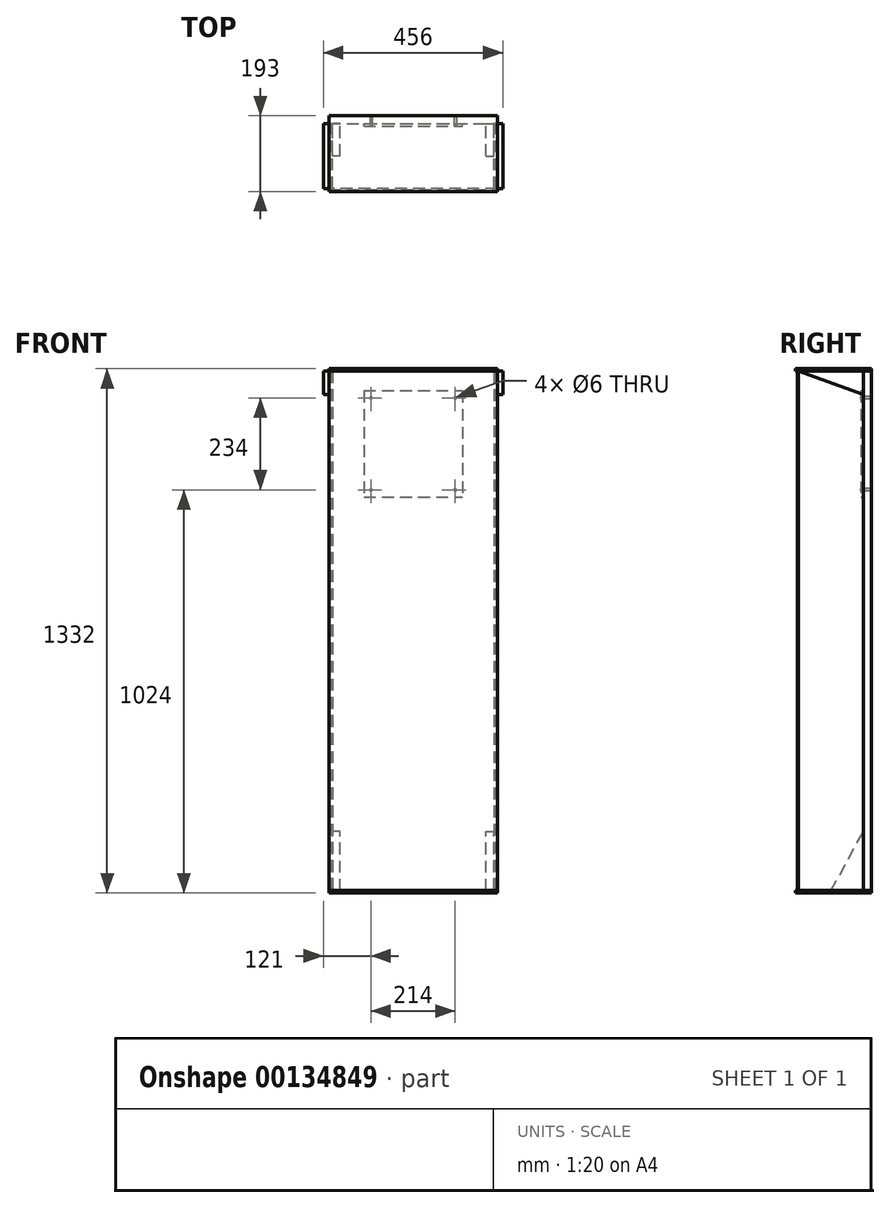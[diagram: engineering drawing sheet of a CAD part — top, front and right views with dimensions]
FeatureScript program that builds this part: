
annotation { "Feature Type Name" : "Feature", "Feature Type Description" : "" }
export const myFeature = defineFeature(function(context is Context, id is Id, definition is map)
    precondition{}
    {
        {
            var Q0;
            Q0=qCreatedBy(makeId("Front.planeOp"),FACE);
            var sketch = newSketch(context, id + "F0", { "sketchPlane" : qUnion([Q0])});
            skLineSegment(sketch, "E0.rect.bottom", {"start": v(-125, 125) * mm, "end": v(125, 125) * mm});
            skLineSegment(sketch, "E0.rect.top", {"start": v(-125, -125) * mm, "end": v(125, -125) * mm});
            skLineSegment(sketch, "E0.rect.left", {"start": v(-125, 125) * mm, "end": v(-125, -125) * mm});
            skLineSegment(sketch, "E0.rect.right", {"start": v(125, 125) * mm, "end": v(125, -125) * mm});
            skPoint(sketch, "E0.rect.middle", {"position": v(0, 0) * mm});
            skSolve(sketch);
        }
        {
            var Q0;
            Q0=qSketchRegion(id+"F0",true);
            extrude(context, id + "F1", {"entities" : qUnion([Q0]), "depth" : 6 * mm});
        }
        {
            var Q0;
            Q0=makeQuery(id+"F1.opExtrude","CAP_FACE",FACE,{"disambiguationData":[OSD([sQuery(id+"F0.wireOp",EDGE,"E0.rect.bottom"),sQuery(id+"F0.wireOp",EDGE,"E0.rect.top"),sQuery(id+"F0.wireOp",EDGE,"E0.rect.left"),sQuery(id+"F0.wireOp",EDGE,"E0.rect.right")])],"isStart":true});
            var sketch = newSketch(context, id + "F2", { "sketchPlane" : qUnion([Q0])});
            skLineSegment(sketch, "E1.rect.bottom", {"start": v(214, 175) * mm, "end": v(-214, 175) * mm});
            skLineSegment(sketch, "E1.rect.top", {"start": v(214, -1145) * mm, "end": v(-214, -1145) * mm});
            skLineSegment(sketch, "E1.rect.left", {"start": v(214, 175) * mm, "end": v(214, -1145) * mm});
            skLineSegment(sketch, "E1.rect.right", {"start": v(-214, 175) * mm, "end": v(-214, -1145) * mm});
            skPoint(sketch, "E1.rect.middle", {"position": v(0, -485) * mm});
            skSolve(sketch);
        }
        {
            var Q0;
            Q0=qSketchRegion(id+"F2",true);
            extrude(context, id + "F3", {"entities" : qUnion([Q0]), "depth" : 20 * mm});
        }
        {
            var Q0;
            Q0=makeQuery(id+"F3.opExtrude","SWEPT_FACE",FACE,{"disambiguationData":[OSD([sQuery(id+"F2.wireOp",EDGE,"E1.rect.bottom")])]});
            var sketch = newSketch(context, id + "F4", { "sketchPlane" : qUnion([Q0])});
            skLineSegment(sketch, "E2.bottom", {"start": v(-214, 20) * mm, "end": v(214, 20) * mm});
            skLineSegment(sketch, "E2.top", {"start": v(-214, -173) * mm, "end": v(214, -173) * mm});
            skLineSegment(sketch, "E2.left", {"start": v(-214, 20) * mm, "end": v(-214, -173) * mm});
            skLineSegment(sketch, "E2.right", {"start": v(214, 20) * mm, "end": v(214, -173) * mm});
            skSolve(sketch);
        }
        {
            var Q0;
            Q0=qSketchRegion(id+"F4",true);
            extrude(context, id + "F5", {"entities" : qUnion([Q0]), "depth" : 6 * mm});
        }
        {
            var Q0;
            Q0=makeQuery(id+"F3.opExtrude","CAP_FACE",FACE,{"disambiguationData":[OSD([sQuery(id+"F2.wireOp",EDGE,"E1.rect.bottom"),sQuery(id+"F2.wireOp",EDGE,"E1.rect.top"),sQuery(id+"F2.wireOp",EDGE,"E1.rect.left"),sQuery(id+"F2.wireOp",EDGE,"E1.rect.right")])],"isStart":true});
            var sketch = newSketch(context, id + "F6", { "sketchPlane" : qUnion([Q0])});
            skLineSegment(sketch, "E3.bottom", {"start": v(-208, 175) * mm, "end": v(-205, 175) * mm});
            skLineSegment(sketch, "E3.top", {"start": v(-208, -1145) * mm, "end": v(-205, -1145) * mm});
            skLineSegment(sketch, "E3.left", {"start": v(-208, 175) * mm, "end": v(-208, -1145) * mm});
            skLineSegment(sketch, "E3.right", {"start": v(-205, 175) * mm, "end": v(-205, -1145) * mm});
            skSolve(sketch);
        }
        {
            var Q0;
            Q0=qSketchRegion(id+"F6",true);
            extrude(context, id + "F7", {"entities" : qUnion([Q0]), "depth" : 165 * mm});
        }
        {
            var Q0;
            Q0=makeQuery(id+"F7.opExtrude","SWEPT_BODY",BODY,{"disambiguationData":[OSD([sQuery(id+"F6.wireOp",EDGE,"E3.bottom"),sQuery(id+"F6.wireOp",EDGE,"E3.top"),sQuery(id+"F6.wireOp",EDGE,"E3.left"),sQuery(id+"F6.wireOp",EDGE,"E3.right")])]});
            var Q1;
            Q1=qCreatedBy(makeId("Right.planeOp"),FACE);
            mirror(context, id + "F8", {"entities" : qUnion([Q0]), "mirrorPlane" : qUnion([Q1])});
        }
        {
            var Q0;
            Q0=makeQuery(id+"F5.opExtrude","CAP_FACE",FACE,{"disambiguationData":[OSD([sQuery(id+"F4.wireOp",EDGE,"E2.bottom"),sQuery(id+"F4.wireOp",EDGE,"E2.top"),sQuery(id+"F4.wireOp",EDGE,"E2.left"),sQuery(id+"F4.wireOp",EDGE,"E2.right")])],"isStart":true});
            var Q1;
            Q1=makeQuery(id+"F3.opExtrude","SWEPT_FACE",FACE,{"disambiguationData":[OSD([sQuery(id+"F2.wireOp",EDGE,"E1.rect.top")])]});
            cPlane(context, id + "F9", {"entities" : qUnion([Q0, Q1]), "cplaneType" : CPlaneType.MID_PLANE, "offset" : 150 * mm, "width" : 150 * mm, "height" : 150 * mm});
        }
        {
            var Q0;
            Q0=makeQuery(id+"F5.opExtrude","SWEPT_BODY",BODY,{"disambiguationData":[OSD([sQuery(id+"F4.wireOp",EDGE,"E2.bottom"),sQuery(id+"F4.wireOp",EDGE,"E2.top"),sQuery(id+"F4.wireOp",EDGE,"E2.left"),sQuery(id+"F4.wireOp",EDGE,"E2.right")])]});
            var Q1;
            Q1=qCreatedBy(id+"F9.planeOp",FACE);
            mirror(context, id + "F10", {"entities" : qUnion([Q0]), "mirrorPlane" : qUnion([Q1])});
        }
        {
            var Q0;
            Q0=makeQuery(id+"F5.opExtrude","CAP_FACE",FACE,{"disambiguationData":[OSD([sQuery(id+"F4.wireOp",EDGE,"E2.bottom"),sQuery(id+"F4.wireOp",EDGE,"E2.top"),sQuery(id+"F4.wireOp",EDGE,"E2.left"),sQuery(id+"F4.wireOp",EDGE,"E2.right")])],"isStart":true});
            var sketch = newSketch(context, id + "F11", { "sketchPlane" : qUnion([Q0])});
            skLineSegment(sketch, "E4.0", {"start": v(-208, 165) * mm, "end": v(-205, 165) * mm});
            skLineSegment(sketch, "E5.0", {"start": v(208, 165) * mm, "end": v(205, 165) * mm});
            skLineSegment(sketch, "E6.bottom", {"start": v(-214, 165) * mm, "end": v(214, 165) * mm});
            skLineSegment(sketch, "E6.top", {"start": v(-214, 168) * mm, "end": v(214, 168) * mm});
            skLineSegment(sketch, "E6.left", {"start": v(-214, 165) * mm, "end": v(-214, 168) * mm});
            skLineSegment(sketch, "E6.right", {"start": v(214, 165) * mm, "end": v(214, 168) * mm});
            skSolve(sketch);
        }
        {
            var Q0;
            Q0=qSketchRegion(id+"F11",true);
            var Q1;
            Q1=makeQuery(id+"F10.opPattern","COPY",FACE,{"derivedFrom":makeQuery(id+"F5.opExtrude","CAP_FACE",FACE,{"disambiguationData":[OSD([sQuery(id+"F4.wireOp",EDGE,"E2.bottom"),sQuery(id+"F4.wireOp",EDGE,"E2.top"),sQuery(id+"F4.wireOp",EDGE,"E2.left"),sQuery(id+"F4.wireOp",EDGE,"E2.right")])],"isStart":true}),"instanceName":"1"});
            extrude(context, id + "F12", {"entities" : qUnion([Q0]), "endBound" : BoundingType.UP_TO_SURFACE, "endBoundEntityFace" : qUnion([Q1]), "depth" : 25 * mm});
        }
        {
            var Q0;
            Q0=makeQuery(id+"F7.opExtrude","SWEPT_FACE",FACE,{"disambiguationData":[OSD([sQuery(id+"F6.wireOp",EDGE,"E3.right")])]});
            var sketch = newSketch(context, id + "F13", { "sketchPlane" : qUnion([Q0])});
            skLineSegment(sketch, "E7", {"start": v(0, -995) * mm, "end": v(0, -1145) * mm});
            skLineSegment(sketch, "E8", {"start": v(0, -1145) * mm, "end": v(-82.5, -1145) * mm});
            skLineSegment(sketch, "E9", {"start": v(-82.5, -1145) * mm, "end": v(0, -995) * mm});
            skSolve(sketch);
        }
        {
            var Q0;
            Q0=qSketchRegion(id+"F13",true);
            extrude(context, id + "F14", {"entities" : qUnion([Q0]), "depth" : 20 * mm});
        }
        {
            var Q0;
            Q0=makeQuery(id+"F14.opExtrude","SWEPT_BODY",BODY,{"disambiguationData":[OSD([sQuery(id+"F13.wireOp",EDGE,"E7"),sQuery(id+"F13.wireOp",EDGE,"E8"),sQuery(id+"F13.wireOp",EDGE,"E9")])]});
            var Q1;
            Q1=qCreatedBy(makeId("Right.planeOp"),FACE);
            mirror(context, id + "F15", {"entities" : qUnion([Q0]), "mirrorPlane" : qUnion([Q1])});
        }
        {
            var Q0;
            Q0=makeQuery(id+"F7.opExtrude","SWEPT_FACE",FACE,{"disambiguationData":[OSD([sQuery(id+"F6.wireOp",EDGE,"E3.left")])]});
            var sketch = newSketch(context, id + "F16", { "sketchPlane" : qUnion([Q0])});
            skLineSegment(sketch, "E10", {"start": v(0, 175) * mm, "end": v(165, 175) * mm});
            skLineSegment(sketch, "E11", {"start": v(165, 175) * mm, "end": v(0, 114.94) * mm});
            skLineSegment(sketch, "E12", {"start": v(0, 114.94) * mm, "end": v(0, 175) * mm});
            skSolve(sketch);
        }
        {
            var Q0;
            Q0=makeQuery(id+"F16.imprint","IMPRINT",FACE,{"disambiguationData":[TD([[makeQuery(id+"F16.imprint","IMPRINT",EDGE,{"derivedFrom":sQuery(id+"F16.wireOp",EDGE,"E10")}),1.0]])]});
            extrude(context, id + "F17", {"entities" : qUnion([Q0]), "depth" : 20 * mm});
        }
        {
            var Q0;
            Q0=makeQuery(id+"F17.opExtrude","SWEPT_BODY",BODY,{"disambiguationData":[OSD([sQuery(id+"F16.wireOp",EDGE,"E10"),sQuery(id+"F16.wireOp",EDGE,"E11"),sQuery(id+"F16.wireOp",EDGE,"E12")])]});
            var Q1;
            Q1=qCreatedBy(makeId("Right.planeOp"),FACE);
            mirror(context, id + "F18", {"entities" : qUnion([Q0]), "mirrorPlane" : qUnion([Q1])});
        }
        {
            var Q0;
            Q0=makeQuery(id+"F1.opExtrude","SWEPT_FACE",FACE,{"disambiguationData":[OSD([sQuery(id+"F0.wireOp",EDGE,"E0.rect.top")])]});
            var sketch = newSketch(context, id + "F19", { "sketchPlane" : qUnion([Q0])});
            skLineSegment(sketch, "E13.0.0", {"start": v(-125, 0) * mm, "end": v(125, 0) * mm});
            skLineSegment(sketch, "E13.0.1", {"start": v(125, 0) * mm, "end": v(125, 6) * mm});
            skLineSegment(sketch, "E13.0.2", {"start": v(125, 6) * mm, "end": v(-125, 6) * mm});
            skLineSegment(sketch, "E13.0.3", {"start": v(-125, 6) * mm, "end": v(-125, 0) * mm});
            skSolve(sketch);
        }
        {
            var Q0;
            Q0=qSketchRegion(id+"F19",true);
            extrude(context, id + "F20", {"entities" : qUnion([Q0]), "operationType" : NewBodyOperationType.ADD, "depth" : 20 * mm});
        }
        {
            var Q0;
            Q0=makeQuery(id+"F20.boolean.opBoolean","MERGE",FACE,{"derivedFrom":[makeQuery(id+"F1.opExtrude","CAP_FACE",FACE,{"disambiguationData":[OSD([sQuery(id+"F0.wireOp",EDGE,"E0.rect.bottom"),sQuery(id+"F0.wireOp",EDGE,"E0.rect.top"),sQuery(id+"F0.wireOp",EDGE,"E0.rect.left"),sQuery(id+"F0.wireOp",EDGE,"E0.rect.right")])],"isStart":false}),makeQuery(id+"F20.opExtrude","SWEPT_FACE",FACE,{"disambiguationData":[OSD([sQuery(id+"F19.wireOp",EDGE,"E13.0.2")])]})]});
            var sketch = newSketch(context, id + "F21", { "sketchPlane" : qUnion([Q0])});
            skCircle(sketch, "E14", {"center": v(-107, 107) * mm, "radius": 3 * mm});
            skCircle(sketch, "E15", {"center": v(-107, -127) * mm, "radius": 3 * mm});
            skCircle(sketch, "E16.MirrorC", {"center": v(107, 107) * mm, "radius": 3 * mm});
            skCircle(sketch, "E17.MirrorC", {"center": v(107, -127) * mm, "radius": 3 * mm});
            skSolve(sketch);
        }
        {
            var Q0;
            Q0=qSketchRegion(id+"F21",true);
            var Q1;
            Q1=qCreatedBy(makeId("Front.planeOp"),FACE);
            extrude(context, id + "F22", {"entities" : qUnion([Q0]), "operationType" : NewBodyOperationType.REMOVE, "endBound" : BoundingType.THROUGH_ALL, "oppositeDirection" : true, "endBoundEntityFace" : qUnion([Q1]), "depth" : 25 * mm});
        }
    });
